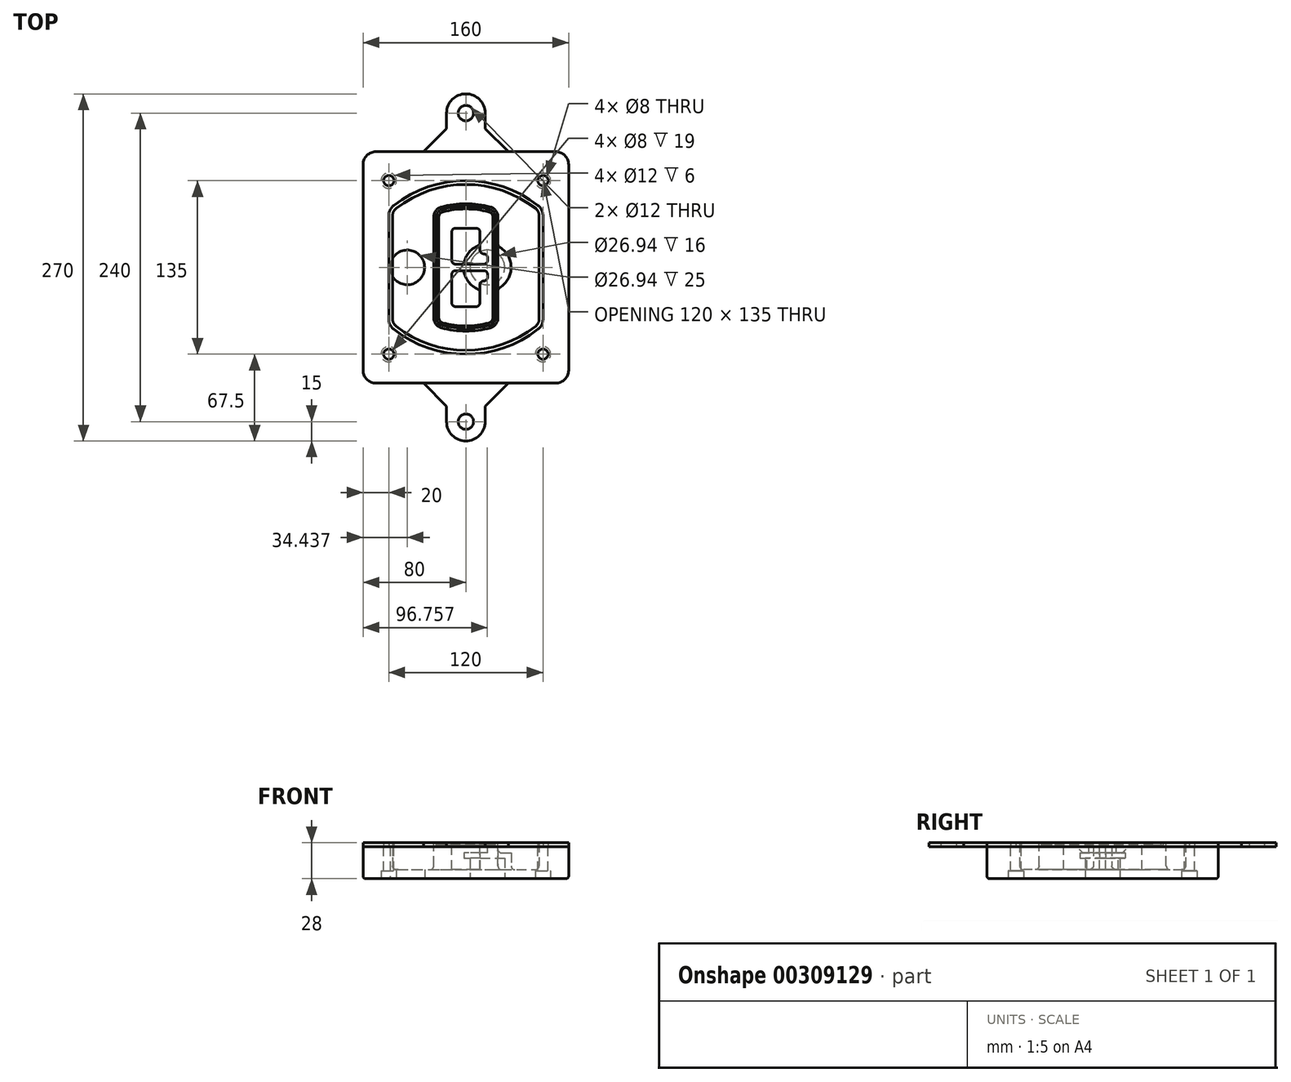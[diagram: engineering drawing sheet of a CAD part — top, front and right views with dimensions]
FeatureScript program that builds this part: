
annotation { "Feature Type Name" : "Feature", "Feature Type Description" : "" }
export const myFeature = defineFeature(function(context is Context, id is Id, definition is map)
    precondition{}
    {
        {
            var Q0;
            Q0=qCreatedBy(makeId("Top.planeOp"),FACE);
            var sketch = newSketch(context, id + "F0", { "sketchPlane" : qUnion([Q0])});
            skPoint(sketch, "E0.rect.middle", {"position": v(0, 0) * mm});
            skLineSegment(sketch, "E1.bottom", {"start": v(-70, -90) * mm, "end": v(70, -90) * mm});
            skLineSegment(sketch, "E1.top", {"start": v(-70, 90) * mm, "end": v(70, 90) * mm});
            skLineSegment(sketch, "E1.left", {"start": v(-80, -80) * mm, "end": v(-80, 80) * mm});
            skLineSegment(sketch, "E1.right", {"start": v(80, -80) * mm, "end": v(80, 80) * mm});
            skLineSegment(sketch, "E2", {"start": v(-80, 90) * mm, "end": v(80, -90) * mm, "construction": true});
            skLineSegment(sketch, "E3", {"start": v(80, 90) * mm, "end": v(-80, -90) * mm, "construction": true});
            skCircle(sketch, "E4", {"center": v(-60, 67.5) * mm, "radius": 4 * mm});
            skCircle(sketch, "E5", {"center": v(60, 67.5) * mm, "radius": 4 * mm});
            skCircle(sketch, "E6", {"center": v(60, -67.5) * mm, "radius": 4 * mm});
            skCircle(sketch, "E7", {"center": v(-60, -67.5) * mm, "radius": 4 * mm});
            skLineSegment(sketch, "E8", {"start": v(-60, 67.5) * mm, "end": v(60, 67.5) * mm, "construction": true});
            skLineSegment(sketch, "E9", {"start": v(60, 67.5) * mm, "end": v(60, -67.5) * mm, "construction": true});
            skLineSegment(sketch, "E10", {"start": v(60, -67.5) * mm, "end": v(-60, -67.5) * mm, "construction": true});
            skLineSegment(sketch, "E11", {"start": v(-60, -67.5) * mm, "end": v(-60, 67.5) * mm, "construction": true});
            skLineSegment(sketch, "E12", {"start": v(-60, 40.3) * mm, "end": v(-60, -40.3) * mm});
            skLineSegment(sketch, "E13", {"start": v(60, 40.3) * mm, "end": v(60, -40.3) * mm});
            skArc(sketch, "E14", {"start": v(56.15, 48.18) * mm, "mid": v(0, 67.5) * mm, "end": v(-56.15, 48.18) * mm});
            skArc(sketch, "E15", {"start": v(-56.15, -48.18) * mm, "mid": v(0, -67.5) * mm, "end": v(56.15, -48.18) * mm});
            skLineSegment(sketch, "E16", {"start": v(-60, 0) * mm, "end": v(60, 0) * mm, "construction": true});
            skPoint(sketch, "E17.visualSharp", {"position": v(-60, -45) * mm});
            skArc(sketch, "E17.filletArc", {"start": v(-60, -40.3) * mm, "mid": v(-58.99, -44.68) * mm, "end": v(-56.15, -48.18) * mm});
            skPoint(sketch, "E18.visualSharp", {"position": v(-60, 45) * mm});
            skArc(sketch, "E18.filletArc", {"start": v(-56.15, 48.18) * mm, "mid": v(-58.99, 44.68) * mm, "end": v(-60, 40.3) * mm});
            skPoint(sketch, "E19.visualSharp", {"position": v(60, 45) * mm});
            skArc(sketch, "E19.filletArc", {"start": v(60, 40.3) * mm, "mid": v(58.99, 44.68) * mm, "end": v(56.15, 48.18) * mm});
            skPoint(sketch, "E20.visualSharp", {"position": v(60, -45) * mm});
            skArc(sketch, "E20.filletArc", {"start": v(56.15, -48.18) * mm, "mid": v(58.99, -44.68) * mm, "end": v(60, -40.3) * mm});
            skPoint(sketch, "E21.visualSharp", {"position": v(-80, 90) * mm});
            skArc(sketch, "E21.filletArc", {"start": v(-70, 90) * mm, "mid": v(-77.07, 87.07) * mm, "end": v(-80, 80) * mm});
            skPoint(sketch, "E22.visualSharp", {"position": v(80, 90) * mm});
            skArc(sketch, "E22.filletArc", {"start": v(80, 80) * mm, "mid": v(77.07, 87.07) * mm, "end": v(70, 90) * mm});
            skPoint(sketch, "E23.visualSharp", {"position": v(80, -90) * mm});
            skArc(sketch, "E23.filletArc", {"start": v(70, -90) * mm, "mid": v(77.07, -87.07) * mm, "end": v(80, -80) * mm});
            skPoint(sketch, "E24.visualSharp", {"position": v(-80, -90) * mm});
            skArc(sketch, "E24.filletArc", {"start": v(-80, -80) * mm, "mid": v(-77.07, -87.07) * mm, "end": v(-70, -90) * mm});
            skArc(sketch, "E25.0", {"start": v(57, 40.3) * mm, "mid": v(56.3, 43.36) * mm, "end": v(54.3, 45.81) * mm});
            skLineSegment(sketch, "E25.1", {"start": v(57, 40.3) * mm, "end": v(57, -40.3) * mm});
            skArc(sketch, "E25.2", {"start": v(54.3, -45.81) * mm, "mid": v(56.3, -43.36) * mm, "end": v(57, -40.3) * mm});
            skArc(sketch, "E25.3", {"start": v(-54.3, -45.81) * mm, "mid": v(0, -64.5) * mm, "end": v(54.3, -45.81) * mm});
            skArc(sketch, "E25.4", {"start": v(-57, -40.3) * mm, "mid": v(-56.3, -43.36) * mm, "end": v(-54.3, -45.81) * mm});
            skArc(sketch, "E25.5", {"start": v(54.3, 45.81) * mm, "mid": v(0, 64.5) * mm, "end": v(-54.3, 45.81) * mm});
            skLineSegment(sketch, "E25.6", {"start": v(-57, 40.3) * mm, "end": v(-57, -40.3) * mm});
            skArc(sketch, "E25.7", {"start": v(-54.3, 45.81) * mm, "mid": v(-56.3, 43.36) * mm, "end": v(-57, 40.3) * mm});
            skArc(sketch, "E26.0", {"start": v(-58.62, 51.33) * mm, "mid": v(-62.58, 46.43) * mm, "end": v(-64, 40.3) * mm});
            skArc(sketch, "E26.1", {"start": v(58.62, 51.33) * mm, "mid": v(0, 71.5) * mm, "end": v(-58.62, 51.33) * mm});
            skArc(sketch, "E26.2", {"start": v(64, 40.3) * mm, "mid": v(62.58, 46.43) * mm, "end": v(58.62, 51.33) * mm});
            skLineSegment(sketch, "E26.3", {"start": v(64, 40.3) * mm, "end": v(64, -40.3) * mm});
            skArc(sketch, "E26.4", {"start": v(58.62, -51.33) * mm, "mid": v(62.58, -46.43) * mm, "end": v(64, -40.3) * mm});
            skLineSegment(sketch, "E26.5", {"start": v(-64, 40.3) * mm, "end": v(-64, -40.3) * mm});
            skArc(sketch, "E26.6", {"start": v(-58.62, -51.33) * mm, "mid": v(0, -71.5) * mm, "end": v(58.62, -51.33) * mm});
            skArc(sketch, "E26.7", {"start": v(-64, -40.3) * mm, "mid": v(-62.58, -46.43) * mm, "end": v(-58.62, -51.33) * mm});
            skSolve(sketch);
        }
        {
            var Q0;
            Q0=makeQuery(id+"F0.imprint","IMPRINT",FACE,{"disambiguationData":[TD([[makeQuery(id+"F0.imprint","IMPRINT",EDGE,{"derivedFrom":sQuery(id+"F0.wireOp",EDGE,"E1.bottom")}),1.0]])]});
            var Q1;
            Q1=makeQuery(id+"F0.imprint","IMPRINT",FACE,{"disambiguationData":[TD([[makeQuery(id+"F0.imprint","IMPRINT",EDGE,{"derivedFrom":sQuery(id+"F0.wireOp",EDGE,"E12")}),1.0]])]});
            var Q2;
            Q2=makeQuery(id+"F0.imprint","IMPRINT",FACE,{"disambiguationData":[TD([[makeQuery(id+"F0.imprint","IMPRINT",EDGE,{"derivedFrom":sQuery(id+"F0.wireOp",EDGE,"E25.0")}),1.0]])]});
            var Q3;
            Q3=makeQuery(id+"F0.imprint","IMPRINT",FACE,{"disambiguationData":[TD([[makeQuery(id+"F0.imprint","IMPRINT",EDGE,{"derivedFrom":sQuery(id+"F0.wireOp",EDGE,"E12")}),-1.0]])]});
            extrude(context, id + "F1", {"entities" : qUnion([Q0, Q1, Q2, Q3]), "oppositeDirection" : true, "depth" : 25 * mm});
        }
        {
            var Q0;
            Q0=makeQuery(id+"F0.imprint","IMPRINT",FACE,{"disambiguationData":[TD([[makeQuery(id+"F0.imprint","IMPRINT",EDGE,{"derivedFrom":sQuery(id+"F0.wireOp",EDGE,"E12")}),1.0]])]});
            extrude(context, id + "F2", {"entities" : qUnion([Q0]), "operationType" : NewBodyOperationType.ADD, "depth" : 3 * mm});
        }
        {
            var Q0;
            Q0=makeQuery(id+"F0.imprint","IMPRINT",FACE,{"disambiguationData":[TD([[makeQuery(id+"F0.imprint","IMPRINT",EDGE,{"derivedFrom":sQuery(id+"F0.wireOp",EDGE,"E25.0")}),1.0]])]});
            extrude(context, id + "F3", {"entities" : qUnion([Q0]), "operationType" : NewBodyOperationType.REMOVE, "oppositeDirection" : true, "depth" : 18 * mm});
        }
        {
            var Q0;
            Q0=makeQuery(id+"F2.opExtrude","CAP_FACE",FACE,{"disambiguationData":[OSD([sQuery(id+"F0.wireOp",EDGE,"E12"),sQuery(id+"F0.wireOp",EDGE,"E13"),sQuery(id+"F0.wireOp",EDGE,"E14"),sQuery(id+"F0.wireOp",EDGE,"E15"),sQuery(id+"F0.wireOp",EDGE,"E17.filletArc"),sQuery(id+"F0.wireOp",EDGE,"E18.filletArc"),sQuery(id+"F0.wireOp",EDGE,"E19.filletArc"),sQuery(id+"F0.wireOp",EDGE,"E20.filletArc"),sQuery(id+"F0.wireOp",EDGE,"E25.0"),sQuery(id+"F0.wireOp",EDGE,"E25.1"),sQuery(id+"F0.wireOp",EDGE,"E25.2"),sQuery(id+"F0.wireOp",EDGE,"E25.3"),sQuery(id+"F0.wireOp",EDGE,"E25.4"),sQuery(id+"F0.wireOp",EDGE,"E25.5"),sQuery(id+"F0.wireOp",EDGE,"E25.6"),sQuery(id+"F0.wireOp",EDGE,"E25.7")])],"isStart":false});
            var sketch = newSketch(context, id + "F4", { "sketchPlane" : qUnion([Q0])});
            skArc(sketch, "E27.0", {"start": v(-19.08, -46.97) * mm, "mid": v(0, -49.5) * mm, "end": v(19.08, -46.97) * mm});
            skArc(sketch, "E28.0", {"start": v(19.08, 46.97) * mm, "mid": v(0, 49.5) * mm, "end": v(-19.08, 46.97) * mm});
            skLineSegment(sketch, "E29", {"start": v(-25, 39.25) * mm, "end": v(-25, -39.25) * mm});
            skLineSegment(sketch, "E30", {"start": v(25, 39.25) * mm, "end": v(25, -39.25) * mm});
            skLineSegment(sketch, "E31", {"start": v(-25, 45.1) * mm, "end": v(25, 45.1) * mm, "construction": true});
            skLineSegment(sketch, "E32", {"start": v(-25, -45.1) * mm, "end": v(25, -45.1) * mm, "construction": true});
            skPoint(sketch, "E33.visualSharp", {"position": v(-25, 45.1) * mm});
            skArc(sketch, "E33.filletArc", {"start": v(-19.08, 46.97) * mm, "mid": v(-23.35, 44.11) * mm, "end": v(-25, 39.25) * mm});
            skPoint(sketch, "E34.visualSharp", {"position": v(25, 45.1) * mm});
            skArc(sketch, "E34.filletArc", {"start": v(25, 39.25) * mm, "mid": v(23.35, 44.11) * mm, "end": v(19.08, 46.97) * mm});
            skPoint(sketch, "E35.visualSharp", {"position": v(25, -45.1) * mm});
            skArc(sketch, "E35.filletArc", {"start": v(19.08, -46.97) * mm, "mid": v(23.35, -44.11) * mm, "end": v(25, -39.25) * mm});
            skPoint(sketch, "E36.visualSharp", {"position": v(-25, -45.1) * mm});
            skArc(sketch, "E36.filletArc", {"start": v(-25, -39.25) * mm, "mid": v(-23.35, -44.11) * mm, "end": v(-19.08, -46.97) * mm});
            skArc(sketch, "E37.0", {"start": v(54.3, 45.81) * mm, "mid": v(0, 64.5) * mm, "end": v(-54.3, 45.81) * mm});
            skArc(sketch, "E37.1", {"start": v(-54.3, 45.81) * mm, "mid": v(-56.3, 43.36) * mm, "end": v(-57, 40.3) * mm});
            skLineSegment(sketch, "E37.2", {"start": v(-57, 40.3) * mm, "end": v(-57, -40.3) * mm});
            skArc(sketch, "E37.3", {"start": v(-57, -40.3) * mm, "mid": v(-56.3, -43.36) * mm, "end": v(-54.3, -45.81) * mm});
            skArc(sketch, "E37.4", {"start": v(-54.3, -45.81) * mm, "mid": v(0, -64.5) * mm, "end": v(54.3, -45.81) * mm});
            skArc(sketch, "E37.5", {"start": v(54.3, -45.81) * mm, "mid": v(56.3, -43.36) * mm, "end": v(57, -40.3) * mm});
            skLineSegment(sketch, "E37.6", {"start": v(57, 40.3) * mm, "end": v(57, -40.3) * mm});
            skArc(sketch, "E37.7", {"start": v(57, 40.3) * mm, "mid": v(56.3, 43.36) * mm, "end": v(54.3, 45.81) * mm});
            skLineSegment(sketch, "E38.0", {"start": v(23, 39.25) * mm, "end": v(23, -39.25) * mm});
            skArc(sketch, "E38.1", {"start": v(18.56, -45.04) * mm, "mid": v(21.76, -42.9) * mm, "end": v(23, -39.25) * mm});
            skArc(sketch, "E38.2", {"start": v(-18.56, -45.04) * mm, "mid": v(0, -47.5) * mm, "end": v(18.56, -45.04) * mm});
            skArc(sketch, "E38.3", {"start": v(-23, -39.25) * mm, "mid": v(-21.76, -42.9) * mm, "end": v(-18.56, -45.04) * mm});
            skLineSegment(sketch, "E38.4", {"start": v(-23, 39.25) * mm, "end": v(-23, -39.25) * mm});
            skArc(sketch, "E38.5", {"start": v(23, 39.25) * mm, "mid": v(21.76, 42.9) * mm, "end": v(18.56, 45.04) * mm});
            skArc(sketch, "E38.6", {"start": v(-18.56, 45.04) * mm, "mid": v(-21.76, 42.9) * mm, "end": v(-23, 39.25) * mm});
            skArc(sketch, "E38.7", {"start": v(18.56, 45.04) * mm, "mid": v(0, 47.5) * mm, "end": v(-18.56, 45.04) * mm});
            skArc(sketch, "E39.0", {"start": v(21, 39.25) * mm, "mid": v(20.18, 41.68) * mm, "end": v(18.04, 43.1) * mm});
            skLineSegment(sketch, "E39.1", {"start": v(21, 39.25) * mm, "end": v(21, -39.25) * mm});
            skArc(sketch, "E39.2", {"start": v(18.04, -43.1) * mm, "mid": v(20.18, -41.68) * mm, "end": v(21, -39.25) * mm});
            skArc(sketch, "E39.3", {"start": v(-18.04, -43.1) * mm, "mid": v(0, -45.5) * mm, "end": v(18.04, -43.1) * mm});
            skArc(sketch, "E39.4", {"start": v(-21, -39.25) * mm, "mid": v(-20.18, -41.68) * mm, "end": v(-18.04, -43.1) * mm});
            skArc(sketch, "E39.5", {"start": v(18.04, 43.1) * mm, "mid": v(0, 45.5) * mm, "end": v(-18.04, 43.1) * mm});
            skLineSegment(sketch, "E39.6", {"start": v(-21, 39.25) * mm, "end": v(-21, -39.25) * mm});
            skArc(sketch, "E39.7", {"start": v(-18.04, 43.1) * mm, "mid": v(-20.18, 41.68) * mm, "end": v(-21, 39.25) * mm});
            skLineSegment(sketch, "E40", {"start": v(-25, 0) * mm, "end": v(25, 0) * mm, "construction": true});
            skLineSegment(sketch, "E41", {"start": v(-11, 5.5) * mm, "end": v(-11, 27.5) * mm});
            skLineSegment(sketch, "E42", {"start": v(-8, 30.5) * mm, "end": v(8, 30.5) * mm});
            skLineSegment(sketch, "E43", {"start": v(11, 27.5) * mm, "end": v(11, 13.5) * mm});
            skLineSegment(sketch, "E44", {"start": v(14, 10.5) * mm, "end": v(14, 10.5) * mm});
            skLineSegment(sketch, "E45", {"start": v(17, 7.5) * mm, "end": v(17, 5.5) * mm});
            skLineSegment(sketch, "E46", {"start": v(14, 2.5) * mm, "end": v(-8, 2.5) * mm});
            skPoint(sketch, "E47.visualSharp", {"position": v(-11, 30.5) * mm});
            skArc(sketch, "E47.filletArc", {"start": v(-8, 30.5) * mm, "mid": v(-10.12, 29.62) * mm, "end": v(-11, 27.5) * mm});
            skPoint(sketch, "E48.visualSharp", {"position": v(11, 30.5) * mm});
            skArc(sketch, "E48.filletArc", {"start": v(11, 27.5) * mm, "mid": v(10.12, 29.62) * mm, "end": v(8, 30.5) * mm});
            skPoint(sketch, "E49.visualSharp", {"position": v(11, 10.5) * mm});
            skArc(sketch, "E49.filletArc", {"start": v(11, 13.5) * mm, "mid": v(11.88, 11.38) * mm, "end": v(14, 10.5) * mm});
            skPoint(sketch, "E50.visualSharp", {"position": v(17, 10.5) * mm});
            skArc(sketch, "E50.filletArc", {"start": v(17, 7.5) * mm, "mid": v(16.12, 9.62) * mm, "end": v(14, 10.5) * mm});
            skPoint(sketch, "E51.visualSharp", {"position": v(17, 2.5) * mm});
            skArc(sketch, "E51.filletArc", {"start": v(14, 2.5) * mm, "mid": v(16.12, 3.38) * mm, "end": v(17, 5.5) * mm});
            skPoint(sketch, "E52.visualSharp", {"position": v(-11, 2.5) * mm});
            skArc(sketch, "E52.filletArc", {"start": v(-11, 5.5) * mm, "mid": v(-10.12, 3.38) * mm, "end": v(-8, 2.5) * mm});
            skLineSegment(sketch, "E53.0.MirrorCS", {"start": v(14, -2.5) * mm, "end": v(-8, -2.5) * mm});
            skArc(sketch, "E54.0.MirrorCS", {"start": v(-11, -5.5) * mm, "mid": v(-10.12, -3.38) * mm, "end": v(-8, -2.5) * mm});
            skLineSegment(sketch, "E55.0.MirrorCS", {"start": v(-11, -5.5) * mm, "end": v(-11, -27.5) * mm});
            skArc(sketch, "E56.0.MirrorCS", {"start": v(-8, -30.5) * mm, "mid": v(-10.12, -29.62) * mm, "end": v(-11, -27.5) * mm});
            skLineSegment(sketch, "E57.0.MirrorCS", {"start": v(-8, -30.5) * mm, "end": v(8, -30.5) * mm});
            skArc(sketch, "E58.0.MirrorCS", {"start": v(11, -27.5) * mm, "mid": v(10.12, -29.62) * mm, "end": v(8, -30.5) * mm});
            skLineSegment(sketch, "E59.0.MirrorCS", {"start": v(11, -27.5) * mm, "end": v(11, -13.5) * mm});
            skArc(sketch, "E60.0.MirrorCS", {"start": v(11, -13.5) * mm, "mid": v(11.88, -11.38) * mm, "end": v(14, -10.5) * mm});
            skArc(sketch, "E61.0.MirrorCS", {"start": v(17, -7.5) * mm, "mid": v(16.12, -9.62) * mm, "end": v(14, -10.5) * mm});
            skLineSegment(sketch, "E62.0.MirrorCS", {"start": v(17, -7.5) * mm, "end": v(17, -5.5) * mm});
            skArc(sketch, "E63.0.MirrorCS", {"start": v(14, -2.5) * mm, "mid": v(16.12, -3.38) * mm, "end": v(17, -5.5) * mm});
            skSolve(sketch);
        }
        {
            var Q0;
            Q0=makeQuery(id+"F4.imprint","IMPRINT",FACE,{"disambiguationData":[TD([[makeQuery(id+"F4.imprint","IMPRINT",EDGE,{"derivedFrom":sQuery(id+"F4.wireOp",EDGE,"E27.0")}),1.0]])]});
            var Q1;
            Q1=makeQuery(id+"F4.imprint","IMPRINT",FACE,{"disambiguationData":[TD([[makeQuery(id+"F4.imprint","IMPRINT",EDGE,{"derivedFrom":sQuery(id+"F4.wireOp",EDGE,"E38.0")}),-1.0]])]});
            var Q2;
            Q2=makeQuery(id+"F4.imprint","IMPRINT",FACE,{"disambiguationData":[TD([[makeQuery(id+"F4.imprint","IMPRINT",EDGE,{"derivedFrom":sQuery(id+"F4.wireOp",EDGE,"E39.0")}),1.0]])]});
            extrude(context, id + "F5", {"entities" : qUnion([Q0, Q1, Q2]), "operationType" : NewBodyOperationType.ADD, "endBound" : BoundingType.UP_TO_NEXT, "oppositeDirection" : true, "depth" : 25 * mm});
        }
        {
            var Q0;
            Q0=makeQuery(id+"F4.imprint","IMPRINT",FACE,{"disambiguationData":[TD([[makeQuery(id+"F4.imprint","IMPRINT",EDGE,{"derivedFrom":sQuery(id+"F4.wireOp",EDGE,"E38.0")}),-1.0]])]});
            extrude(context, id + "F6", {"entities" : qUnion([Q0]), "operationType" : NewBodyOperationType.REMOVE, "oppositeDirection" : true, "depth" : 2 * mm});
        }
        {
            var Q0;
            Q0=makeQuery(id+"F1.opExtrude","CAP_FACE",FACE,{"disambiguationData":[OSD([sQuery(id+"F0.wireOp",EDGE,"E1.bottom"),sQuery(id+"F0.wireOp",EDGE,"E1.top"),sQuery(id+"F0.wireOp",EDGE,"E1.left"),sQuery(id+"F0.wireOp",EDGE,"E1.right"),sQuery(id+"F0.wireOp",EDGE,"E4"),sQuery(id+"F0.wireOp",EDGE,"E5"),sQuery(id+"F0.wireOp",EDGE,"E6"),sQuery(id+"F0.wireOp",EDGE,"E7"),sQuery(id+"F0.wireOp",EDGE,"E21.filletArc"),sQuery(id+"F0.wireOp",EDGE,"E22.filletArc"),sQuery(id+"F0.wireOp",EDGE,"E23.filletArc"),sQuery(id+"F0.wireOp",EDGE,"E24.filletArc")])],"isStart":false});
            var sketch = newSketch(context, id + "F7", { "sketchPlane" : qUnion([Q0])});
            skCircle(sketch, "E64", {"center": v(16.76, 0) * mm, "radius": 13.47 * mm});
            skCircle(sketch, "E65", {"center": v(-45.56, 0) * mm, "radius": 13.47 * mm});
            skLineSegment(sketch, "E66", {"start": v(80, 0) * mm, "end": v(-80, 0) * mm});
            skCircle(sketch, "E67", {"center": v(16.76, 0) * mm, "radius": 18.47 * mm});
            skCircle(sketch, "E68", {"center": v(60, -67.5) * mm, "radius": 6 * mm});
            skCircle(sketch, "E69", {"center": v(-60, -67.5) * mm, "radius": 6 * mm});
            skCircle(sketch, "E70", {"center": v(-60, 67.5) * mm, "radius": 6 * mm});
            skCircle(sketch, "E71", {"center": v(60, 67.5) * mm, "radius": 6 * mm});
            skSolve(sketch);
        }
        {
            var Q0;
            {var subQ1=sQuery(id+"F7.wireOp",EDGE,"E66");var subQ4=sQuery(id+"F7.wireOp",EDGE,"E64");var subQ6=makeQuery(id+"F7.imprint","INTERSECT",VERTEX,{"disambiguationData":[OD(0.0)],"derivedFrom":[subQ4,subQ1]});Q0=makeQuery(id+"F7.imprint","IMPRINT",FACE,{"disambiguationData":[TD([[makeQuery(id+"F7.imprint","IMPRINT",EDGE,{"disambiguationData":[TD([[subQ6,-1.0]])],"derivedFrom":subQ4}),-1.0]])]});}
            var Q1;
            {var subQ0=sQuery(id+"F7.wireOp",EDGE,"E66");var subQ1=sQuery(id+"F7.wireOp",EDGE,"E64");var subQ3=makeQuery(id+"F7.imprint","INTERSECT",VERTEX,{"disambiguationData":[OD(0.0)],"derivedFrom":[subQ1,subQ0]});Q1=makeQuery(id+"F7.imprint","IMPRINT",FACE,{"disambiguationData":[TD([[makeQuery(id+"F7.imprint","IMPRINT",EDGE,{"disambiguationData":[TD([[subQ3,-1.0]])],"derivedFrom":subQ1}),1.0]])]});}
            var Q2;
            {var subQ0=sQuery(id+"F7.wireOp",EDGE,"E66");var subQ1=sQuery(id+"F7.wireOp",EDGE,"E64");var subQ3=makeQuery(id+"F7.imprint","INTERSECT",VERTEX,{"disambiguationData":[OD(0.0)],"derivedFrom":[subQ1,subQ0]});Q2=makeQuery(id+"F7.imprint","IMPRINT",FACE,{"disambiguationData":[TD([[makeQuery(id+"F7.imprint","IMPRINT",EDGE,{"disambiguationData":[TD([[subQ3,1.0]])],"derivedFrom":subQ1}),1.0]])]});}
            var Q3;
            {var subQ1=sQuery(id+"F7.wireOp",EDGE,"E66");var subQ4=sQuery(id+"F7.wireOp",EDGE,"E64");var subQ6=makeQuery(id+"F7.imprint","INTERSECT",VERTEX,{"disambiguationData":[OD(0.0)],"derivedFrom":[subQ4,subQ1]});Q3=makeQuery(id+"F7.imprint","IMPRINT",FACE,{"disambiguationData":[TD([[makeQuery(id+"F7.imprint","IMPRINT",EDGE,{"disambiguationData":[TD([[subQ6,1.0]])],"derivedFrom":subQ4}),-1.0]])]});}
            extrude(context, id + "F8", {"entities" : qUnion([Q0, Q1, Q2, Q3]), "operationType" : NewBodyOperationType.ADD, "oppositeDirection" : true, "depth" : 20 * mm});
        }
        {
            var Q0;
            {var subQ0=sQuery(id+"F7.wireOp",EDGE,"E66");var subQ1=sQuery(id+"F7.wireOp",EDGE,"E64");var subQ3=makeQuery(id+"F7.imprint","INTERSECT",VERTEX,{"disambiguationData":[OD(0.0)],"derivedFrom":[subQ1,subQ0]});Q0=makeQuery(id+"F7.imprint","IMPRINT",FACE,{"disambiguationData":[TD([[makeQuery(id+"F7.imprint","IMPRINT",EDGE,{"disambiguationData":[TD([[subQ3,-1.0]])],"derivedFrom":subQ1}),1.0]])]});}
            var Q1;
            {var subQ0=sQuery(id+"F7.wireOp",EDGE,"E66");var subQ1=sQuery(id+"F7.wireOp",EDGE,"E64");var subQ3=makeQuery(id+"F7.imprint","INTERSECT",VERTEX,{"disambiguationData":[OD(0.0)],"derivedFrom":[subQ1,subQ0]});Q1=makeQuery(id+"F7.imprint","IMPRINT",FACE,{"disambiguationData":[TD([[makeQuery(id+"F7.imprint","IMPRINT",EDGE,{"disambiguationData":[TD([[subQ3,1.0]])],"derivedFrom":subQ1}),1.0]])]});}
            extrude(context, id + "F9", {"entities" : qUnion([Q0, Q1]), "operationType" : NewBodyOperationType.REMOVE, "oppositeDirection" : true, "depth" : 16 * mm});
        }
        {
            var Q0;
            {var subQ0=sQuery(id+"F7.wireOp",EDGE,"E66");var subQ1=sQuery(id+"F7.wireOp",EDGE,"E65");var subQ3=makeQuery(id+"F7.imprint","INTERSECT",VERTEX,{"disambiguationData":[OD(0.0)],"derivedFrom":[subQ1,subQ0]});Q0=makeQuery(id+"F7.imprint","IMPRINT",FACE,{"disambiguationData":[TD([[makeQuery(id+"F7.imprint","IMPRINT",EDGE,{"disambiguationData":[TD([[subQ3,-1.0]])],"derivedFrom":subQ1}),1.0]])]});}
            var Q1;
            {var subQ0=sQuery(id+"F7.wireOp",EDGE,"E66");var subQ1=sQuery(id+"F7.wireOp",EDGE,"E65");var subQ3=makeQuery(id+"F7.imprint","INTERSECT",VERTEX,{"disambiguationData":[OD(0.0)],"derivedFrom":[subQ1,subQ0]});Q1=makeQuery(id+"F7.imprint","IMPRINT",FACE,{"disambiguationData":[TD([[makeQuery(id+"F7.imprint","IMPRINT",EDGE,{"disambiguationData":[TD([[subQ3,1.0]])],"derivedFrom":subQ1}),1.0]])]});}
            extrude(context, id + "F10", {"entities" : qUnion([Q0, Q1]), "operationType" : NewBodyOperationType.REMOVE, "oppositeDirection" : true, "depth" : 25 * mm});
        }
        {
            var Q0;
            Q0=makeQuery(id+"F7.imprint","IMPRINT",FACE,{"disambiguationData":[TD([[makeQuery(id+"F7.imprint","IMPRINT",EDGE,{"derivedFrom":sQuery(id+"F7.wireOp",EDGE,"E68")}),1.0]])]});
            var Q1;
            Q1=makeQuery(id+"F7.imprint","IMPRINT",FACE,{"disambiguationData":[TD([[makeQuery(id+"F7.imprint","IMPRINT",EDGE,{"derivedFrom":makeQuery(id+"F1.opExtrude","CAP_EDGE",EDGE,{"disambiguationData":[OSD([sQuery(id+"F0.wireOp",EDGE,"E5")])],"isStart":false})}),-1.0]])]});
            var Q2;
            Q2=makeQuery(id+"F7.imprint","IMPRINT",FACE,{"disambiguationData":[TD([[makeQuery(id+"F7.imprint","IMPRINT",EDGE,{"derivedFrom":sQuery(id+"F7.wireOp",EDGE,"E69")}),1.0]])]});
            var Q3;
            Q3=makeQuery(id+"F7.imprint","IMPRINT",FACE,{"disambiguationData":[TD([[makeQuery(id+"F7.imprint","IMPRINT",EDGE,{"derivedFrom":makeQuery(id+"F1.opExtrude","CAP_EDGE",EDGE,{"disambiguationData":[OSD([sQuery(id+"F0.wireOp",EDGE,"E4")])],"isStart":false})}),-1.0]])]});
            var Q4;
            Q4=makeQuery(id+"F7.imprint","IMPRINT",FACE,{"disambiguationData":[TD([[makeQuery(id+"F7.imprint","IMPRINT",EDGE,{"derivedFrom":sQuery(id+"F7.wireOp",EDGE,"E70")}),1.0]])]});
            var Q5;
            Q5=makeQuery(id+"F7.imprint","IMPRINT",FACE,{"disambiguationData":[TD([[makeQuery(id+"F7.imprint","IMPRINT",EDGE,{"derivedFrom":makeQuery(id+"F1.opExtrude","CAP_EDGE",EDGE,{"disambiguationData":[OSD([sQuery(id+"F0.wireOp",EDGE,"E7")])],"isStart":false})}),-1.0]])]});
            var Q6;
            Q6=makeQuery(id+"F7.imprint","IMPRINT",FACE,{"disambiguationData":[TD([[makeQuery(id+"F7.imprint","IMPRINT",EDGE,{"derivedFrom":sQuery(id+"F7.wireOp",EDGE,"E71")}),1.0]])]});
            var Q7;
            Q7=makeQuery(id+"F7.imprint","IMPRINT",FACE,{"disambiguationData":[TD([[makeQuery(id+"F7.imprint","IMPRINT",EDGE,{"derivedFrom":makeQuery(id+"F1.opExtrude","CAP_EDGE",EDGE,{"disambiguationData":[OSD([sQuery(id+"F0.wireOp",EDGE,"E6")])],"isStart":false})}),-1.0]])]});
            extrude(context, id + "F11", {"entities" : qUnion([Q0, Q1, Q2, Q3, Q4, Q5, Q6, Q7]), "operationType" : NewBodyOperationType.REMOVE, "oppositeDirection" : true, "depth" : 6 * mm});
        }
        {
            var Q0;
            Q0=makeQuery(id+"F9.boolean.opBoolean","COPY",FACE,{"derivedFrom":makeQuery(id+"F9.opExtrude","CAP_FACE",FACE,{"disambiguationData":[OSD([sQuery(id+"F7.wireOp",EDGE,"E64")])],"isStart":false})});
            var sketch = newSketch(context, id + "F12", { "sketchPlane" : qUnion([Q0])});
            skArc(sketch, "E72.0", {"start": v(11, 17.55) * mm, "mid": v(2.57, 11.82) * mm, "end": v(-1.54, 2.5) * mm});
            skArc(sketch, "E72.1", {"start": v(-1.54, -2.5) * mm, "mid": v(2.57, -11.82) * mm, "end": v(11, -17.55) * mm});
            skLineSegment(sketch, "E73", {"start": v(-1.54, -2.5) * mm, "end": v(14, -2.5) * mm});
            skLineSegment(sketch, "E74.0", {"start": v(14, 2.5) * mm, "end": v(-1.54, 2.5) * mm});
            skArc(sketch, "E74.1", {"start": v(14, 2.5) * mm, "mid": v(16.12, 3.38) * mm, "end": v(17, 5.5) * mm});
            skLineSegment(sketch, "E74.2", {"start": v(17, 7.5) * mm, "end": v(17, 5.5) * mm});
            skArc(sketch, "E74.3", {"start": v(17, 7.5) * mm, "mid": v(16.12, 9.62) * mm, "end": v(14, 10.5) * mm});
            skArc(sketch, "E74.4", {"start": v(11, 13.5) * mm, "mid": v(11.88, 11.38) * mm, "end": v(14, 10.5) * mm});
            skLineSegment(sketch, "E74.5", {"start": v(11, 17.55) * mm, "end": v(11, 13.5) * mm});
            skLineSegment(sketch, "E74.7", {"start": v(14, -2.5) * mm, "end": v(-1.54, -2.5) * mm});
            skArc(sketch, "E74.8", {"start": v(14, -2.5) * mm, "mid": v(16.12, -3.38) * mm, "end": v(17, -5.5) * mm});
            skLineSegment(sketch, "E74.9", {"start": v(17, -7.5) * mm, "end": v(17, -5.5) * mm});
            skArc(sketch, "E74.10", {"start": v(17, -7.5) * mm, "mid": v(16.12, -9.62) * mm, "end": v(14, -10.5) * mm});
            skArc(sketch, "E74.11", {"start": v(11, -13.5) * mm, "mid": v(11.88, -11.38) * mm, "end": v(14, -10.5) * mm});
            skLineSegment(sketch, "E74.12", {"start": v(11, -17.55) * mm, "end": v(11, -13.5) * mm});
            skPoint(sketch, "E75.orphan", {"position": v(11, -27.5) * mm});
            skPoint(sketch, "E76.orphan", {"position": v(-8, -2.5) * mm});
            skPoint(sketch, "E77.orphan", {"position": v(-8, 2.5) * mm});
            skPoint(sketch, "E78.orphan", {"position": v(11, 27.5) * mm});
            skSolve(sketch);
        }
        {
            var Q0;
            {var subQ7=sQuery(id+"F12.wireOp",EDGE,"E72.0");var subQ14=sQuery(id+"F12.wireOp",EDGE,"E72.1");var subQ16=sQuery(id+"F12.wireOp",EDGE,"E74.1");var subQ18=sQuery(id+"F12.wireOp",EDGE,"E74.8");Q0=qUnion([makeQuery(id+"F12.imprint","IMPRINT",FACE,{"disambiguationData":[TD([[makeQuery(id+"F12.imprint","IMPRINT",EDGE,{"derivedFrom":subQ7}),1.0]])]}),makeQuery(id+"F12.imprint","IMPRINT",FACE,{"disambiguationData":[TD([[makeQuery(id+"F12.imprint","IMPRINT",EDGE,{"derivedFrom":subQ14}),1.0]])]}),makeQuery(id+"F12.imprint","IMPRINT",FACE,{"disambiguationData":[TD([[makeQuery(id+"F12.imprint","IMPRINT",EDGE,{"derivedFrom":subQ16}),1.0]])]}),makeQuery(id+"F12.imprint","IMPRINT",FACE,{"disambiguationData":[TD([[makeQuery(id+"F12.imprint","IMPRINT",EDGE,{"derivedFrom":subQ18}),-1.0]])]})]);}
            var Q1;
            Q1=makeQuery(id+"F5.boolean.opBoolean","SPLIT",FACE,{"disambiguationData":[TD([makeQuery(id+"F5.opExtrude","SWEPT_FACE",FACE,{"disambiguationData":[OSD([sQuery(id+"F4.wireOp",EDGE,"E41")])]})])],"derivedFrom":makeQuery(id+"F3.boolean.opBoolean","COPY",FACE,{"derivedFrom":makeQuery(id+"F3.opExtrude","CAP_FACE",FACE,{"disambiguationData":[OSD([sQuery(id+"F0.wireOp",EDGE,"E25.0"),sQuery(id+"F0.wireOp",EDGE,"E25.1"),sQuery(id+"F0.wireOp",EDGE,"E25.2"),sQuery(id+"F0.wireOp",EDGE,"E25.3"),sQuery(id+"F0.wireOp",EDGE,"E25.4"),sQuery(id+"F0.wireOp",EDGE,"E25.5"),sQuery(id+"F0.wireOp",EDGE,"E25.6"),sQuery(id+"F0.wireOp",EDGE,"E25.7")])],"isStart":false})})});
            extrude(context, id + "F13", {"entities" : qUnion([Q0]), "operationType" : NewBodyOperationType.REMOVE, "endBound" : BoundingType.UP_TO_SURFACE, "endBoundEntityFace" : qUnion([Q1]), "depth" : 25 * mm});
        }
        {
            var Q0;
            Q0=makeQuery(id+"F3.boolean.opBoolean","COPY",EDGE,{"derivedFrom":makeQuery(id+"F3.opExtrude","CAP_EDGE",EDGE,{"disambiguationData":[OSD([sQuery(id+"F0.wireOp",EDGE,"E25.6")])],"isStart":false})});
            var Q1;
            Q1=makeQuery(id+"F8.boolean.opBoolean","INTERSECT",EDGE,{"derivedFrom":[makeQuery(id+"F5.opExtrude","SWEPT_FACE",FACE,{"disambiguationData":[OSD([sQuery(id+"F4.wireOp",EDGE,"E30")])]}),makeQuery(id+"F8.opExtrude","CAP_FACE",FACE,{"disambiguationData":[OSD([sQuery(id+"F7.wireOp",EDGE,"E67")])],"isStart":false})]});
            var Q2;
            Q2=makeQuery(id+"F8.boolean.opBoolean","INTERSECT",EDGE,{"disambiguationData":[OD(1.0)],"derivedFrom":[makeQuery(id+"F5.opExtrude","SWEPT_FACE",FACE,{"disambiguationData":[OSD([sQuery(id+"F4.wireOp",EDGE,"E30")])]}),makeQuery(id+"F8.opExtrude","SWEPT_FACE",FACE,{"disambiguationData":[OSD([sQuery(id+"F7.wireOp",EDGE,"E67")])]})]});
            var Q3;
            {var subQ0=sQuery(id+"F4.wireOp",EDGE,"E30");Q3=makeQuery(id+"F8.boolean.opBoolean","SPLIT",EDGE,{"disambiguationData":[TD([makeQuery(id+"F5.opExtrude","SWEPT_FACE",FACE,{"disambiguationData":[OSD([sQuery(id+"F4.wireOp",EDGE,"E35.filletArc")])]})])],"derivedFrom":makeQuery(id+"F5.opExtrude","CAP_EDGE",EDGE,{"disambiguationData":[OSD([subQ0])],"isStart":false})});}
            var Q4;
            {var subQ0=sQuery(id+"F0.wireOp",EDGE,"E25.7");var subQ1=sQuery(id+"F0.wireOp",EDGE,"E25.1");var subQ2=sQuery(id+"F0.wireOp",EDGE,"E25.6");var subQ3=sQuery(id+"F0.wireOp",EDGE,"E25.5");var subQ4=sQuery(id+"F0.wireOp",EDGE,"E25.4");var subQ5=sQuery(id+"F0.wireOp",EDGE,"E25.0");var subQ6=sQuery(id+"F0.wireOp",EDGE,"E25.2");var subQ7=sQuery(id+"F0.wireOp",EDGE,"E25.3");Q4=makeQuery(id+"F8.boolean.opBoolean","INTERSECT",EDGE,{"derivedFrom":[makeQuery(id+"F5.boolean.opBoolean","SPLIT",FACE,{"disambiguationData":[TD([makeQuery(id+"F2.opExtrude","SWEPT_FACE",FACE,{"disambiguationData":[OSD([subQ5])]})])],"derivedFrom":makeQuery(id+"F3.boolean.opBoolean","COPY",FACE,{"derivedFrom":makeQuery(id+"F3.opExtrude","CAP_FACE",FACE,{"disambiguationData":[OSD([subQ5,subQ1,subQ6,subQ7,subQ4,subQ3,subQ2,subQ0])],"isStart":false})})}),makeQuery(id+"F8.opExtrude","SWEPT_FACE",FACE,{"disambiguationData":[OSD([sQuery(id+"F7.wireOp",EDGE,"E67")])]})]});}
            var Q5;
            Q5=makeQuery(id+"F8.boolean.opBoolean","INTERSECT",EDGE,{"disambiguationData":[OD(0.0)],"derivedFrom":[makeQuery(id+"F5.opExtrude","SWEPT_FACE",FACE,{"disambiguationData":[OSD([sQuery(id+"F4.wireOp",EDGE,"E30")])]}),makeQuery(id+"F8.opExtrude","SWEPT_FACE",FACE,{"disambiguationData":[OSD([sQuery(id+"F7.wireOp",EDGE,"E67")])]})]});
            fillet(context, id + "F14", {"entities" : qUnion([Q0, Q1, Q2, Q3, Q4, Q5]), "radius" : 3 * mm, "tangentPropagation" : true, "allowEdgeOverflow" : false});
        }
        {
            var Q0;
            Q0=makeQuery(id+"F1.opExtrude","CAP_EDGE",EDGE,{"disambiguationData":[OSD([sQuery(id+"F0.wireOp",EDGE,"E1.bottom")])],"isStart":false});
            fillet(context, id + "F15", {"entities" : qUnion([Q0]), "radius" : 2 * mm, "tangentPropagation" : true, "allowEdgeOverflow" : false});
        }
        {
            var Q0;
            {var subQ0=sQuery(id+"F0.wireOp",EDGE,"E21.filletArc");var subQ1=sQuery(id+"F0.wireOp",EDGE,"E7");var subQ2=sQuery(id+"F0.wireOp",EDGE,"E6");var subQ3=sQuery(id+"F0.wireOp",EDGE,"E5");var subQ4=sQuery(id+"F0.wireOp",EDGE,"E4");var subQ5=sQuery(id+"F0.wireOp",EDGE,"E22.filletArc");var subQ6=sQuery(id+"F0.wireOp",EDGE,"E1.bottom");var subQ7=sQuery(id+"F0.wireOp",EDGE,"E1.right");var subQ8=sQuery(id+"F0.wireOp",EDGE,"E1.top");var subQ9=sQuery(id+"F0.wireOp",EDGE,"E1.left");var subQ10=sQuery(id+"F0.wireOp",EDGE,"E23.filletArc");var subQ11=sQuery(id+"F0.wireOp",EDGE,"E24.filletArc");Q0=makeQuery(id+"F2.boolean.opBoolean","SPLIT",FACE,{"disambiguationData":[TD([makeQuery(id+"F1.opExtrude","SWEPT_FACE",FACE,{"disambiguationData":[OSD([subQ6])]})])],"derivedFrom":makeQuery(id+"F1.opExtrude","CAP_FACE",FACE,{"disambiguationData":[OSD([subQ6,subQ8,subQ9,subQ7,subQ4,subQ3,subQ2,subQ1,subQ0,subQ5,subQ10,subQ11])],"isStart":true})});}
            var sketch = newSketch(context, id + "F16", { "sketchPlane" : qUnion([Q0])});
            skCircle(sketch, "E79", {"center": v(0, 120) * mm, "radius": 6 * mm});
            skLineSegment(sketch, "E80", {"start": v(33, 90) * mm, "end": v(15, 108) * mm});
            skLineSegment(sketch, "E81", {"start": v(15, 108) * mm, "end": v(15, 120) * mm});
            skLineSegment(sketch, "E82", {"start": v(-33, 90) * mm, "end": v(-15, 108) * mm});
            skLineSegment(sketch, "E83", {"start": v(-15, 108) * mm, "end": v(-15, 120) * mm});
            skLineSegment(sketch, "E84", {"start": v(0, 120) * mm, "end": v(0, 0) * mm});
            skArc(sketch, "E85", {"start": v(15, 120) * mm, "mid": v(0, 135) * mm, "end": v(-15, 120) * mm});
            skLineSegment(sketch, "E86", {"start": v(-80, 0) * mm, "end": v(80, 0) * mm, "construction": true});
            skLineSegment(sketch, "E87.MirrorCS", {"start": v(33, -90) * mm, "end": v(15, -108) * mm});
            skLineSegment(sketch, "E88.MirrorCS", {"start": v(-33, -90) * mm, "end": v(-15, -108) * mm});
            skLineSegment(sketch, "E89.MirrorCS", {"start": v(-15, -108) * mm, "end": v(-15, -120) * mm});
            skArc(sketch, "E90.MirrorCS", {"start": v(15, -120) * mm, "mid": v(0, -135) * mm, "end": v(-15, -120) * mm});
            skLineSegment(sketch, "E91.MirrorCS", {"start": v(15, -108) * mm, "end": v(15, -120) * mm});
            skCircle(sketch, "E92.MirrorC", {"center": v(0, -120) * mm, "radius": 6 * mm});
            skSolve(sketch);
        }
        {
            var Q0;
            Q0=makeQuery(id+"F16.imprint","IMPRINT",FACE,{"disambiguationData":[TD([[makeQuery(id+"F16.imprint","IMPRINT",EDGE,{"derivedFrom":sQuery(id+"F16.wireOp",EDGE,"E79")}),-1.0]])]});
            var Q1;
            {var subQ0=sQuery(id+"F16.wireOp",EDGE,"E87.MirrorCS");Q1=makeQuery(id+"F16.imprint","IMPRINT",FACE,{"disambiguationData":[TD([[makeQuery(id+"F16.imprint","IMPRINT",EDGE,{"derivedFrom":subQ0}),-1.0]])]});}
            var Q2;
            Q2=makeQuery(id+"F2.opExtrude","CAP_FACE",FACE,{"disambiguationData":[OSD([sQuery(id+"F0.wireOp",EDGE,"E12"),sQuery(id+"F0.wireOp",EDGE,"E13"),sQuery(id+"F0.wireOp",EDGE,"E14"),sQuery(id+"F0.wireOp",EDGE,"E15"),sQuery(id+"F0.wireOp",EDGE,"E17.filletArc"),sQuery(id+"F0.wireOp",EDGE,"E18.filletArc"),sQuery(id+"F0.wireOp",EDGE,"E19.filletArc"),sQuery(id+"F0.wireOp",EDGE,"E20.filletArc"),sQuery(id+"F0.wireOp",EDGE,"E25.0"),sQuery(id+"F0.wireOp",EDGE,"E25.1"),sQuery(id+"F0.wireOp",EDGE,"E25.2"),sQuery(id+"F0.wireOp",EDGE,"E25.3"),sQuery(id+"F0.wireOp",EDGE,"E25.4"),sQuery(id+"F0.wireOp",EDGE,"E25.5"),sQuery(id+"F0.wireOp",EDGE,"E25.6"),sQuery(id+"F0.wireOp",EDGE,"E25.7")])],"isStart":false});
            extrude(context, id + "F17", {"entities" : qUnion([Q0, Q1]), "endBound" : BoundingType.UP_TO_SURFACE, "endBoundEntityFace" : qUnion([Q2]), "depth" : 25 * mm});
        }
        {
            var Q0;
            {var subQ0=sQuery(id+"F0.wireOp",EDGE,"E21.filletArc");var subQ1=sQuery(id+"F0.wireOp",EDGE,"E7");var subQ2=sQuery(id+"F0.wireOp",EDGE,"E6");var subQ3=sQuery(id+"F0.wireOp",EDGE,"E5");var subQ4=sQuery(id+"F0.wireOp",EDGE,"E4");var subQ5=sQuery(id+"F0.wireOp",EDGE,"E22.filletArc");var subQ6=sQuery(id+"F0.wireOp",EDGE,"E1.bottom");var subQ7=sQuery(id+"F0.wireOp",EDGE,"E1.right");var subQ8=sQuery(id+"F0.wireOp",EDGE,"E1.top");var subQ9=sQuery(id+"F0.wireOp",EDGE,"E1.left");var subQ10=sQuery(id+"F0.wireOp",EDGE,"E23.filletArc");var subQ11=sQuery(id+"F0.wireOp",EDGE,"E24.filletArc");Q0=makeQuery(id+"F2.boolean.opBoolean","SPLIT",FACE,{"disambiguationData":[TD([makeQuery(id+"F1.opExtrude","SWEPT_FACE",FACE,{"disambiguationData":[OSD([subQ6])]})])],"derivedFrom":makeQuery(id+"F1.opExtrude","CAP_FACE",FACE,{"disambiguationData":[OSD([subQ6,subQ8,subQ9,subQ7,subQ4,subQ3,subQ2,subQ1,subQ0,subQ5,subQ10,subQ11])],"isStart":true})});}
            var Q1;
            Q1=makeQuery(id+"F2.opExtrude","CAP_FACE",FACE,{"disambiguationData":[OSD([sQuery(id+"F0.wireOp",EDGE,"E12"),sQuery(id+"F0.wireOp",EDGE,"E13"),sQuery(id+"F0.wireOp",EDGE,"E14"),sQuery(id+"F0.wireOp",EDGE,"E15"),sQuery(id+"F0.wireOp",EDGE,"E17.filletArc"),sQuery(id+"F0.wireOp",EDGE,"E18.filletArc"),sQuery(id+"F0.wireOp",EDGE,"E19.filletArc"),sQuery(id+"F0.wireOp",EDGE,"E20.filletArc"),sQuery(id+"F0.wireOp",EDGE,"E25.0"),sQuery(id+"F0.wireOp",EDGE,"E25.1"),sQuery(id+"F0.wireOp",EDGE,"E25.2"),sQuery(id+"F0.wireOp",EDGE,"E25.3"),sQuery(id+"F0.wireOp",EDGE,"E25.4"),sQuery(id+"F0.wireOp",EDGE,"E25.5"),sQuery(id+"F0.wireOp",EDGE,"E25.6"),sQuery(id+"F0.wireOp",EDGE,"E25.7")])],"isStart":false});
            extrude(context, id + "F18", {"entities" : qUnion([Q0]), "endBound" : BoundingType.UP_TO_SURFACE, "endBoundEntityFace" : qUnion([Q1]), "depth" : 25 * mm});
        }
    });
